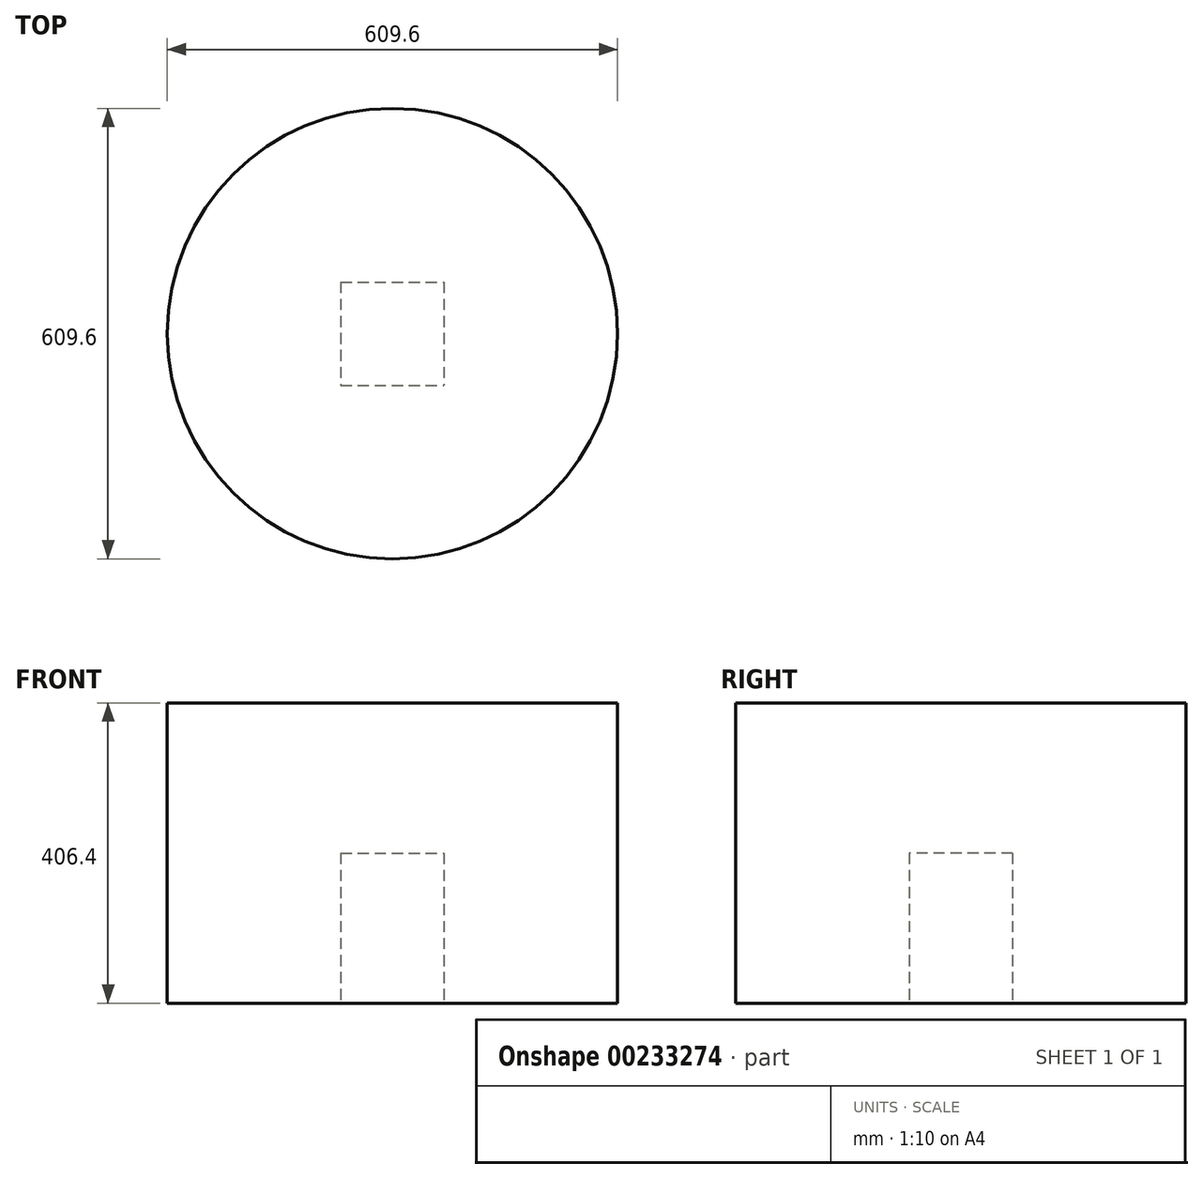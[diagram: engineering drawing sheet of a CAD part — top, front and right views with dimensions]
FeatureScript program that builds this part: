
annotation { "Feature Type Name" : "Feature", "Feature Type Description" : "" }
export const myFeature = defineFeature(function(context is Context, id is Id, definition is map)
    precondition{}
    {
        {
            var Q0;
            Q0=qCreatedBy(makeId("Top.planeOp"),FACE);
            var sketch = newSketch(context, id + "F0", { "sketchPlane" : qUnion([Q0])});
            skCircle(sketch, "E0", {"center": v(-64.03, 93.18) * mm, "radius": 304.8 * mm});
            skLineSegment(sketch, "E1.bottom", {"start": v(-133.88, 163.03) * mm, "end": v(5.82, 163.03) * mm});
            skLineSegment(sketch, "E1.top", {"start": v(-133.88, 23.33) * mm, "end": v(5.82, 23.33) * mm});
            skLineSegment(sketch, "E1.left", {"start": v(-133.88, 163.03) * mm, "end": v(-133.88, 23.33) * mm});
            skLineSegment(sketch, "E1.right", {"start": v(5.82, 163.03) * mm, "end": v(5.82, 23.33) * mm});
            skSolve(sketch);
        }
        {
            var Q0;
            Q0 = qSketchRegion(id + "F0", true);
            extrude(context, id + "F1", {"entities" : qUnion([Q0]), "depth" : 406.4 * mm});
        }
        {
            var Q0;
            Q0=makeQuery(id+"F1.opExtrude","CAP_FACE",FACE,{"disambiguationData":[OSD([sQuery(id+"F0.wireOp",EDGE,"E0")])],"isStart":false});
            var sketch = newSketch(context, id + "F2", { "sketchPlane" : qUnion([Q0])});
            skSolve(sketch);
        }
        {
            var Q0;
            Q0=makeQuery(id+"F2.imprint","IMPRINT",FACE,{"disambiguationData":[TD([[makeQuery(id+"F2.imprint","IMPRINT",EDGE,{"derivedFrom":makeQuery(id+"F1.opExtrude","CAP_EDGE",EDGE,{"disambiguationData":[OSD([sQuery(id+"F0.wireOp",EDGE,"E1.bottom")])],"isStart":false})}),-1.0]])]});
            extrude(context, id + "F3", {"entities" : qUnion([Q0]), "operationType" : NewBodyOperationType.ADD, "oppositeDirection" : true, "depth" : 203.2 * mm});
        }
    });
